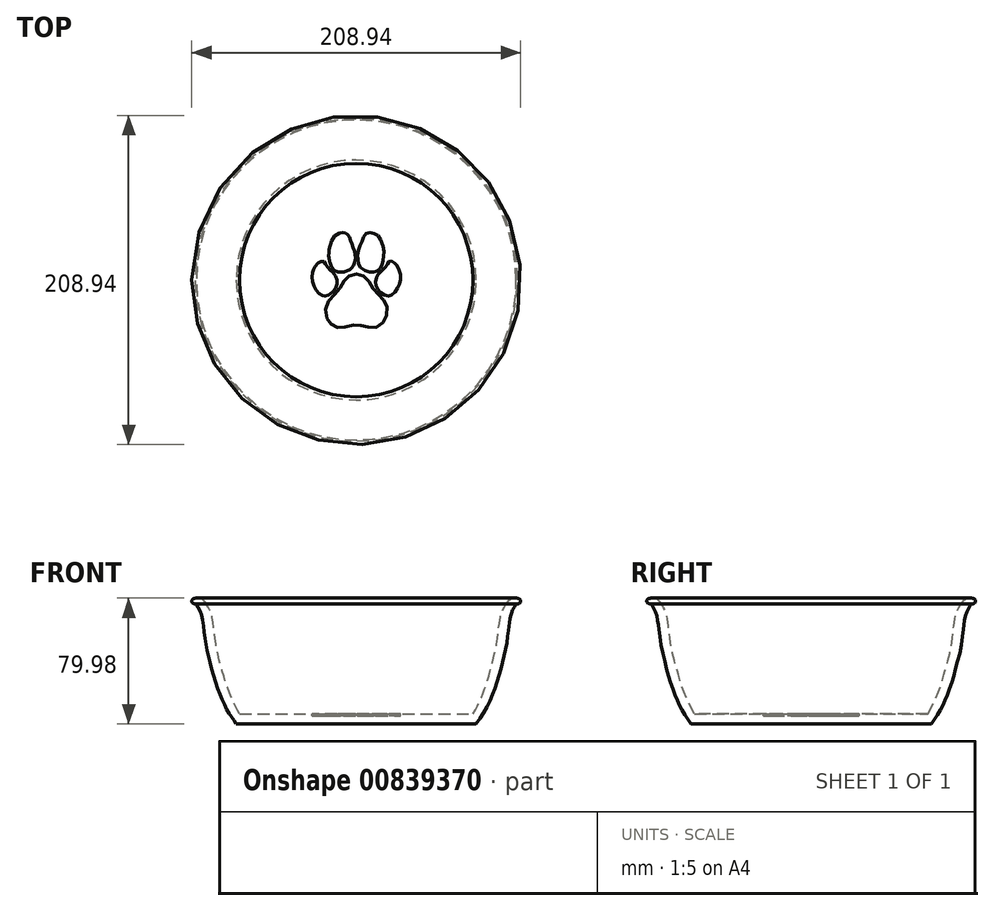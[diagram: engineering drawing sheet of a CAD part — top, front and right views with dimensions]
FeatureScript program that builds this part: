
annotation { "Feature Type Name" : "Feature", "Feature Type Description" : "" }
export const myFeature = defineFeature(function(context is Context, id is Id, definition is map)
    precondition{}
    {
        {
            var Q0;
            Q0=qCreatedBy(makeId("Top.planeOp"),FACE);
            var sketch = newSketch(context, id + "F0", { "sketchPlane" : qUnion([Q0])});
            skCircle(sketch, "E0", {"center": v(0, 0) * mm, "radius": 76.2 * mm});
            skFitSpline(sketch, "E1", {"points": [v(-18.5, -24.43) * mm, v(-19.39, -20.36) * mm, v(-19.01, -15.87) * mm, v(-16.76, -12.12) * mm, v(-14.05, -9.36) * mm, v(-11.66, -7.03) * mm, v(-9.66, -3.9) * mm, v(-8, -0.88) * mm, v(-6.42, 1.08) * mm, v(-3.93, 2.93) * mm, v(-1.22, 3.72) * mm, v(1.65, 3.72) * mm, v(4.4, 2.67) * mm, v(6.93, 0.63) * mm, v(8.29, -1.4) * mm, v(10.17, -4.65) * mm, v(12.06, -7.52) * mm, v(14.47, -9.7) * mm, v(16.41, -11.53) * mm, v(18.24, -13.77) * mm, v(19.33, -16.6) * mm, v(19.42, -20.72) * mm, v(18.73, -24.33) * mm, v(17.21, -26.95) * mm, v(14.25, -29.45) * mm, v(11.05, -30.38) * mm, v(7.33, -29.91) * mm, v(4.53, -29.22) * mm, v(2.32, -28.75) * mm, v(-0.7, -28.58) * mm, v(-3.38, -28.87) * mm, v(-7.56, -29.91) * mm, v(-10.12, -30.38) * mm, v(-13.15, -29.8) * mm, v(-15.59, -28.34) * mm, v(-17.4, -26.42) * mm, v(-18.5, -24.43) * mm]});
            skFitSpline(sketch, "E2", {"points": [v(-27.1, 6.7) * mm, v(-26.34, 8.33) * mm, v(-24.53, 10.54) * mm, v(-22.67, 11.76) * mm, v(-21.16, 12.05) * mm, v(-20.11, 11.47) * mm, v(-19.3, 9.9) * mm, v(-17.79, 7.8) * mm, v(-16.4, 6.23) * mm, v(-14.53, 4.55) * mm, v(-12.9, 2.05) * mm, v(-12.2, -0.75) * mm, v(-12.61, -3.83) * mm, v(-14.41, -7.03) * mm, v(-17.09, -9.18) * mm, v(-19.59, -10.17) * mm, v(-20.75, -10.17) * mm, v(-22.32, -9.47) * mm, v(-24.7, -7.5) * mm, v(-26.4, -4.82) * mm, v(-27.8, -1.21) * mm, v(-28.02, 2.16) * mm, v(-27.56, 5.19) * mm, v(-27.1, 6.7) * mm]});
            skFitSpline(sketch, "E3", {"points": [v(-17.5, 15.21) * mm, v(-17.32, 18.59) * mm, v(-16.97, 20.56) * mm, v(-15.98, 24) * mm, v(-14.41, 27.08) * mm, v(-12.55, 28.88) * mm, v(-9.76, 30.1) * mm, v(-6.97, 29.99) * mm, v(-5.05, 28.42) * mm, v(-3.48, 24.87) * mm, v(-1.85, 20.56) * mm, v(-0.69, 15.8) * mm, v(-1.1, 10.8) * mm, v(-2.78, 7.88) * mm, v(-4.02, 6.7) * mm], "startDerivative": vector(1.62, 50.53) * mm, "endDerivative": vector(-23.35, -19.97) * mm});
            skFitSpline(sketch, "E4", {"points": [v(-4.02, 6.7) * mm, v(-5.84, 5.88) * mm, v(-8.25, 5.08) * mm, v(-10.9, 5) * mm, v(-13.3, 5.72) * mm, v(-15.27, 7.69) * mm, v(-16.47, 10.51) * mm, v(-17.04, 12.81) * mm, v(-17.5, 15.21) * mm], "startDerivative": vector(-15.77, -7.4) * mm, "endDerivative": vector(-3.63, 19.86) * mm});
            skFitSpline(sketch, "E5", {"points": [v(2.66, 8.02) * mm, v(1.62, 9.84) * mm, v(1.06, 12.84) * mm, v(0.88, 16.07) * mm, v(1.86, 20.05) * mm, v(2.98, 23.14) * mm, v(4.1, 26.05) * mm, v(5.56, 28.76) * mm, v(7.71, 30.08) * mm, v(10.62, 29.89) * mm, v(13.05, 28.86) * mm, v(15.3, 25.95) * mm, v(17.36, 19.87) * mm, v(17.45, 16.12) * mm, v(17.17, 13.03) * mm, v(16.33, 9.84) * mm, v(15.24, 7.65) * mm, v(13.62, 6) * mm, v(11.73, 5.16) * mm, v(9.36, 5.01) * mm, v(6.75, 5.54) * mm, v(2.66, 8.02) * mm]});
            skFitSpline(sketch, "E6", {"points": [v(12.76, 1.46) * mm, v(13.58, 3.09) * mm, v(15.2, 4.83) * mm, v(16.37, 6) * mm, v(17.82, 7.4) * mm, v(18.98, 8.9) * mm, v(20.09, 10.65) * mm, v(20.56, 11.46) * mm, v(21.72, 12.04) * mm, v(23, 11.7) * mm, v(24.74, 10.53) * mm, v(26.02, 9.02) * mm, v(27.53, 5.47) * mm, v(28.23, 1.98) * mm, v(27.77, -1.33) * mm, v(26.6, -4.6) * mm, v(24.57, -7.73) * mm, v(22.18, -9.65) * mm, v(20.56, -10.17) * mm, v(18.23, -9.7) * mm, v(15.55, -7.96) * mm, v(13.87, -5.93) * mm, v(12.65, -3.6) * mm, v(12.3, -1.33) * mm, v(12.76, 1.46) * mm]});
            skCircle(sketch, "E7", {"center": v(0, 0) * mm, "radius": 73.03 * mm});
            skSolve(sketch);
        }
        {
            var Q0;
            Q0=makeQuery(id+"F0.imprint","IMPRINT",FACE,{"disambiguationData":[TD([[makeQuery(id+"F0.imprint","IMPRINT",EDGE,{"derivedFrom":sQuery(id+"F0.wireOp",EDGE,"E0")}),1.0]])]});
            var Q1;
            Q1=makeQuery(id+"F0.imprint","IMPRINT",FACE,{"disambiguationData":[TD([[makeQuery(id+"F0.imprint","IMPRINT",EDGE,{"derivedFrom":sQuery(id+"F0.wireOp",EDGE,"E1")}),1.0]])]});
            extrude(context, id + "F1", {"entities" : qUnion([Q0, Q1]), "depth" : 6.35 * mm, "offsetDistance" : 25.4 * mm});
        }
        {
            var Q0;
            Q0=makeQuery(id+"F0.imprint","IMPRINT",FACE,{"disambiguationData":[TD([[makeQuery(id+"F0.imprint","IMPRINT",EDGE,{"derivedFrom":sQuery(id+"F0.wireOp",EDGE,"E2")}),-1.0]])]});
            var Q1;
            Q1=makeQuery(id+"F0.imprint","IMPRINT",FACE,{"disambiguationData":[TD([[makeQuery(id+"F0.imprint","IMPRINT",EDGE,{"derivedFrom":sQuery(id+"F0.wireOp",EDGE,"E3")}),-1.0]])]});
            var Q2;
            Q2=makeQuery(id+"F0.imprint","IMPRINT",FACE,{"disambiguationData":[TD([[makeQuery(id+"F0.imprint","IMPRINT",EDGE,{"derivedFrom":sQuery(id+"F0.wireOp",EDGE,"E5")}),-1.0]])]});
            var Q3;
            Q3=makeQuery(id+"F0.imprint","IMPRINT",FACE,{"disambiguationData":[TD([[makeQuery(id+"F0.imprint","IMPRINT",EDGE,{"derivedFrom":sQuery(id+"F0.wireOp",EDGE,"E6")}),-1.0]])]});
            var Q4;
            Q4=makeQuery(id+"F0.imprint","IMPRINT",FACE,{"disambiguationData":[TD([[makeQuery(id+"F0.imprint","IMPRINT",EDGE,{"derivedFrom":sQuery(id+"F0.wireOp",EDGE,"E1")}),-1.0]])]});
            extrude(context, id + "F2", {"entities" : qUnion([Q0, Q1, Q2, Q3, Q4]), "operationType" : NewBodyOperationType.ADD, "depth" : 5.08 * mm, "offsetDistance" : 25.4 * mm});
        }
        {
            var Q0;
            Q0=qCreatedBy(makeId("Front.planeOp"),FACE);
            var sketch = newSketch(context, id + "F3", { "sketchPlane" : qUnion([Q0])});
            skLineSegment(sketch, "E8", {"start": v(0, 0) * mm, "end": v(-76.2, 0) * mm, "construction": true});
            skLineSegment(sketch, "E9", {"start": v(-76.2, 0) * mm, "end": v(-76.2, 76.2) * mm, "construction": true});
            skLineSegment(sketch, "E10", {"start": v(-76.2, 76.2) * mm, "end": v(-101.6, 76.2) * mm, "construction": true});
            skLineSegment(sketch, "E11", {"start": v(-101.6, 76.2) * mm, "end": v(-76.2, 0) * mm, "construction": true});
            skPoint(sketch, "E12", {"position": v(-69.85, 0) * mm});
            skPoint(sketch, "E13", {"position": v(-95.25, 76.2) * mm});
            skFitSpline(sketch, "E14", {"points": [v(-76.2, 0) * mm, v(-80.82, 6.9) * mm, v(-86.36, 18.2) * mm, v(-92.34, 36.98) * mm, v(-96.03, 54.26) * mm, v(-98.3, 69.54) * mm, v(-101.6, 76.2) * mm], "startDerivative": vector(-34.88, 49.25) * mm, "endDerivative": vector(-29.54, 46.28) * mm});
            skPoint(sketch, "E15", {"position": v(-91.95, 69.54) * mm});
            skPoint(sketch, "E16", {"position": v(-89.68, 54.26) * mm});
            skPoint(sketch, "E17", {"position": v(-85.99, 36.98) * mm});
            skPoint(sketch, "E18", {"position": v(-80.01, 18.2) * mm});
            skPoint(sketch, "E19", {"position": v(-74.47, 6.9) * mm});
            skFitSpline(sketch, "E20", {"points": [v(-69.85, 0) * mm, v(-74.47, 6.9) * mm, v(-80.01, 18.2) * mm, v(-85.99, 36.98) * mm, v(-89.68, 54.26) * mm, v(-91.95, 69.54) * mm, v(-95.25, 76.2) * mm], "startDerivative": vector(-37, 50.74) * mm, "endDerivative": vector(-29.31, 45.89) * mm});
            skFitSpline(sketch, "E21", {"points": [v(-95.25, 76.2) * mm, v(-96.88, 78.42) * mm, v(-99.82, 79.9) * mm, v(-103.73, 79.34) * mm, v(-104.47, 77.93) * mm, v(-103.84, 76.73) * mm, v(-102.39, 76.2) * mm], "startDerivative": vector(-6.67, 10.61) * mm, "endDerivative": vector(9.08, -3.03) * mm});
            skLineSegment(sketch, "E22", {"start": v(-102.39, 76.2) * mm, "end": v(-101.6, 76.2) * mm});
            skLineSegment(sketch, "E23", {"start": v(-76.2, 0) * mm, "end": v(-69.85, 0) * mm});
            skLineSegment(sketch, "E24", {"start": v(0, 0) * mm, "end": v(0, 76.2) * mm, "construction": true});
            skLineSegment(sketch, "E25", {"start": v(-101.6, 76.2) * mm, "end": v(-95.25, 76.2) * mm});
            skSolve(sketch);
        }
        {
            var Q0;
            Q0=makeQuery(id+"F3.imprint","IMPRINT",FACE,{"disambiguationData":[TD([[makeQuery(id+"F3.imprint","IMPRINT",EDGE,{"derivedFrom":sQuery(id+"F3.wireOp",EDGE,"E14")}),-1.0]])]});
            var Q1;
            Q1=sQuery(id+"F3.wireOp",EDGE,"E24");
            revolve(context, id + "F4", {"operationType" : NewBodyOperationType.ADD, "surfaceOperationType" : NewSurfaceOperationType.NEW, "entities" : qUnion([Q0]), "axis" : qUnion([Q1]), "revolveType" : RevolveType.FULL});
        }
        {
            var Q0;
            Q0=makeQuery(id+"F3.imprint","IMPRINT",FACE,{"disambiguationData":[TD([[makeQuery(id+"F3.imprint","IMPRINT",EDGE,{"derivedFrom":sQuery(id+"F3.wireOp",EDGE,"E21")}),1.0]])]});
            var Q1;
            Q1=sQuery(id+"F3.wireOp",EDGE,"E24");
            revolve(context, id + "F5", {"operationType" : NewBodyOperationType.ADD, "surfaceOperationType" : NewSurfaceOperationType.NEW, "entities" : qUnion([Q0]), "axis" : qUnion([Q1]), "revolveType" : RevolveType.FULL});
        }
    });
